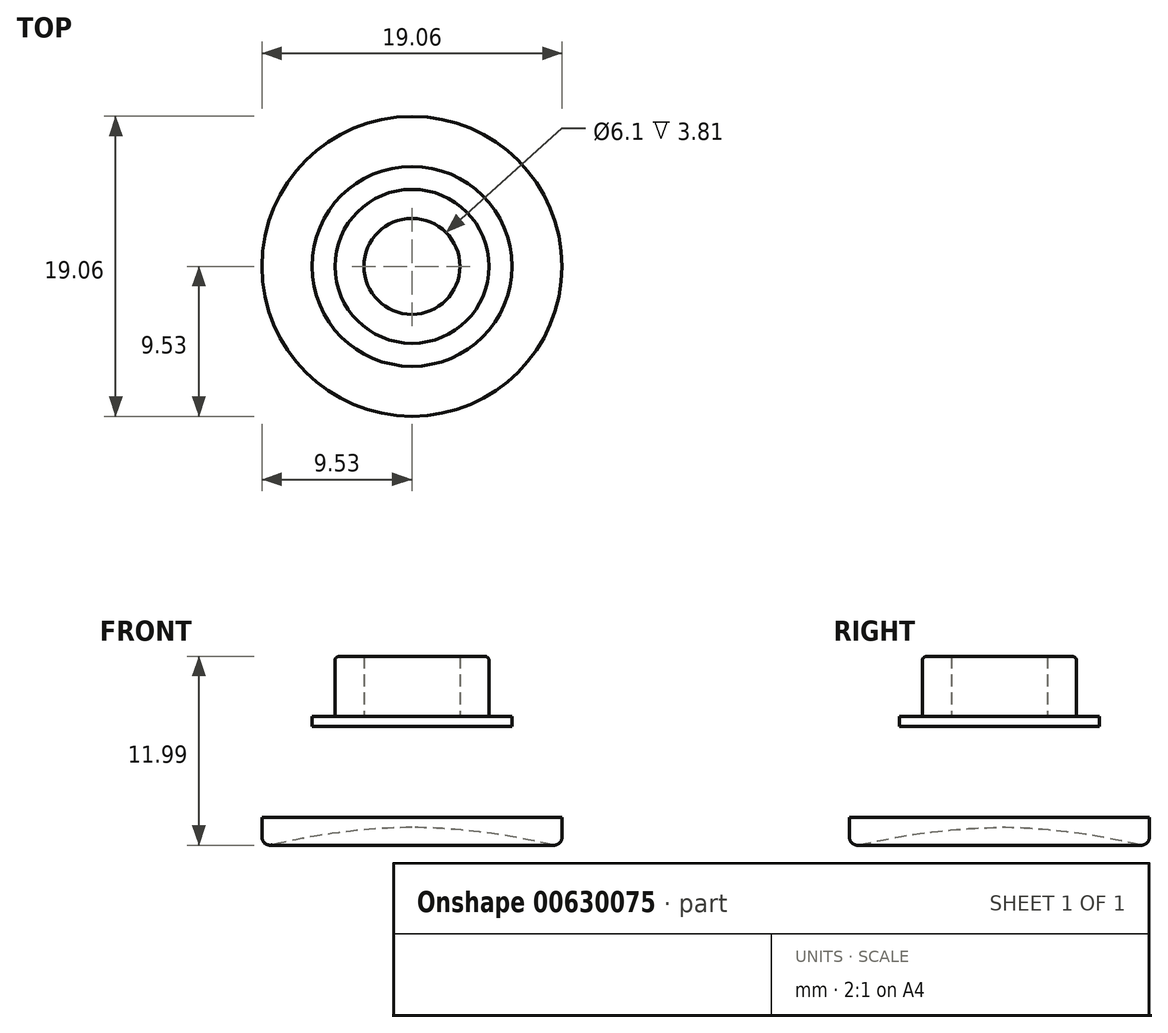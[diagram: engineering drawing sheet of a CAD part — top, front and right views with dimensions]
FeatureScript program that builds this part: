
annotation { "Feature Type Name" : "Feature", "Feature Type Description" : "" }
export const myFeature = defineFeature(function(context is Context, id is Id, definition is map)
    precondition{}
    {
        {
            var Q0;
            Q0=qCreatedBy(makeId("Top.planeOp"),FACE);
            var sketch = newSketch(context, id + "F0", { "sketchPlane" : qUnion([Q0])});
            skCircle(sketch, "E0", {"center": v(0, 0) * mm, "radius": 4.89 * mm});
            skCircle(sketch, "E1", {"center": v(0, 0) * mm, "radius": 3.05 * mm});
            skSolve(sketch);
        }
        {
            var Q0;
            Q0=makeQuery(id+"F0.imprint","IMPRINT",FACE,{"disambiguationData":[TD([[makeQuery(id+"F0.imprint","IMPRINT",EDGE,{"derivedFrom":sQuery(id+"F0.wireOp",EDGE,"E0")}),1.0]])]});
            var Q1;
            Q1=sQuery(id+"F0.wireOp",EDGE,"E0");
            var Q2;
            Q2=sQuery(id+"F0.wireOp",EDGE,"E1");
            extrude(context, id + "F1", {"entities" : qUnion([Q0]), "surfaceEntities" : qUnion([Q1, Q2]), "depth" : 3.8 * mm, "offsetDistance" : 25.4 * mm});
        }
        {
            var Q0;
            Q0=makeQuery(id+"F1.opExtrude","CAP_FACE",FACE,{"disambiguationData":[OSD([sQuery(id+"F0.wireOp",EDGE,"E0"),sQuery(id+"F0.wireOp",EDGE,"E1")])],"isStart":true});
            var sketch = newSketch(context, id + "F2", { "sketchPlane" : qUnion([Q0])});
            skCircle(sketch, "E2", {"center": v(0, 0) * mm, "radius": 6.35 * mm});
            skSolve(sketch);
        }
        {
            var Q0;
            Q0=makeQuery(id+"F2.imprint","IMPRINT",FACE,{"disambiguationData":[TD([[makeQuery(id+"F2.imprint","IMPRINT",EDGE,{"derivedFrom":sQuery(id+"F2.wireOp",EDGE,"E2")}),1.0]])]});
            var Q1;
            Q1=makeQuery(id+"F2.imprint","IMPRINT",FACE,{"disambiguationData":[TD([[makeQuery(id+"F2.imprint","IMPRINT",EDGE,{"derivedFrom":makeQuery(id+"F1.opExtrude","CAP_EDGE",EDGE,{"disambiguationData":[OSD([sQuery(id+"F0.wireOp",EDGE,"E1")])],"isStart":true})}),-1.0]])]});
            var Q2;
            Q2=makeQuery(id+"F2.imprint","IMPRINT",FACE,{"disambiguationData":[TD([[makeQuery(id+"F2.imprint","IMPRINT",EDGE,{"derivedFrom":makeQuery(id+"F1.opExtrude","CAP_EDGE",EDGE,{"disambiguationData":[OSD([sQuery(id+"F0.wireOp",EDGE,"E0")])],"isStart":true})}),-1.0]])]});
            extrude(context, id + "F3", {"entities" : qUnion([Q0, Q1, Q2]), "operationType" : NewBodyOperationType.ADD, "depth" : 0.64 * mm, "offsetDistance" : 25.4 * mm});
        }
        {
            var Q0;
            Q0=qCreatedBy(makeId("Front.planeOp"),FACE);
            var sketch = newSketch(context, id + "F4", { "sketchPlane" : qUnion([Q0])});
            skLineSegment(sketch, "E3", {"start": v(0, -6.42) * mm, "end": v(9.53, -6.42) * mm});
            skLineSegment(sketch, "E4", {"start": v(9.53, -6.42) * mm, "end": v(9.53, -8.32) * mm});
            skLineSegment(sketch, "E5", {"start": v(0, -6.42) * mm, "end": v(0, -7.05) * mm});
            skArc(sketch, "E6", {"start": v(9.53, -8.32) * mm, "mid": v(4.8, -7.4) * mm, "end": v(0, -7.05) * mm});
            skSolve(sketch);
        }
        {
            var Q0;
            Q0=makeQuery(id+"F4.imprint","IMPRINT",FACE,{"disambiguationData":[TD([[makeQuery(id+"F4.imprint","IMPRINT",EDGE,{"derivedFrom":sQuery(id+"F4.wireOp",EDGE,"E3")}),-1.0]])]});
            var Q1;
            Q1=makeQuery(id+"F3.opExtrude","CAP_EDGE",EDGE,{"disambiguationData":[OSD([sQuery(id+"F2.wireOp",EDGE,"E2")])],"isStart":false});
            revolve(context, id + "F5", {"entities" : qUnion([Q0]), "axis" : qUnion([Q1]), "revolveType" : RevolveType.FULL});
        }
        {
            var Q0;
            Q0=makeQuery(id+"F5.opRevolve","SWEPT_EDGE",EDGE,{"disambiguationData":[OSD([sQuery(id+"F4.wireOp",EDGE,"E4"),sQuery(id+"F4.wireOp",EDGE,"E6")])]});
            fillet(context, id + "F6", {"entities" : qUnion([Q0]), "radius" : 0.5 * mm, "tangentPropagation" : true, "allowEdgeOverflow" : false});
        }
        {
            var Q0;
            Q0=makeQuery(id+"F1.opExtrude","CAP_EDGE",EDGE,{"disambiguationData":[OSD([sQuery(id+"F0.wireOp",EDGE,"E0")])],"isStart":false});
            fillet(context, id + "F7", {"entities" : qUnion([Q0]), "radius" : 0.25 * mm, "tangentPropagation" : true, "allowEdgeOverflow" : false});
        }
    });
